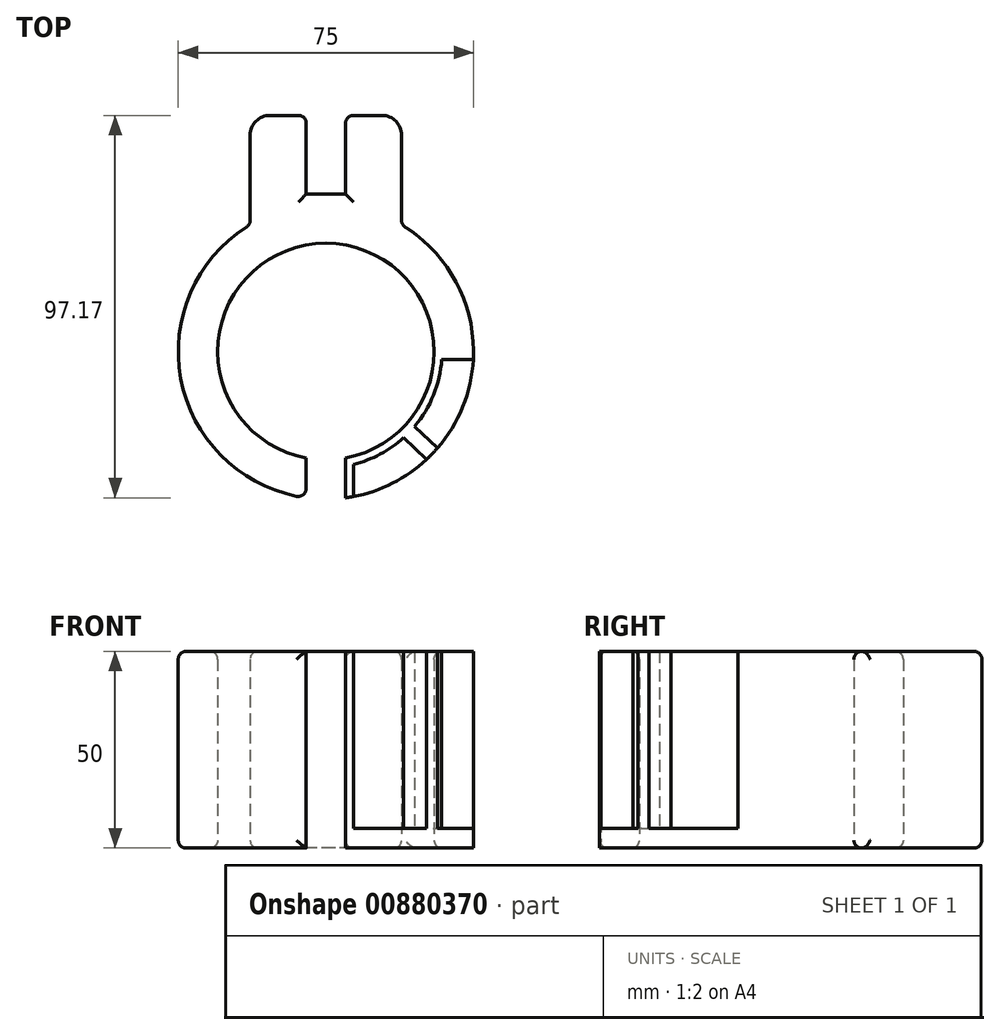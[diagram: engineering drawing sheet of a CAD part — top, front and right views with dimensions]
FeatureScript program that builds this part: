
annotation { "Feature Type Name" : "Feature", "Feature Type Description" : "" }
export const myFeature = defineFeature(function(context is Context, id is Id, definition is map)
    precondition{}
    {
        {
            var Q0;
            Q0=qCreatedBy(makeId("Top.planeOp"),FACE);
            var sketch = newSketch(context, id + "F0", { "sketchPlane" : qUnion([Q0])});
            skArc(sketch, "E0", {"start": v(-19.23, -27.8) * mm, "mid": v(-36.73, -67.54) * mm, "end": v(-5, -97.17) * mm});
            skLineSegment(sketch, "E1", {"start": v(-19.23, -5) * mm, "end": v(-19.23, -27.8) * mm});
            skLineSegment(sketch, "E2", {"start": v(-5, 0) * mm, "end": v(-5, -20) * mm});
            skLineSegment(sketch, "E3", {"start": v(-5, -20) * mm, "end": v(0, -20) * mm});
            skLineSegment(sketch, "E4", {"start": v(-14.23, 0) * mm, "end": v(-5, 0) * mm});
            skLineSegment(sketch, "E5.MirrorCS", {"start": v(19.23, -5) * mm, "end": v(19.23, -27.8) * mm});
            skLineSegment(sketch, "E6.MirrorCS", {"start": v(5, 0) * mm, "end": v(5, -20) * mm});
            skLineSegment(sketch, "E7.MirrorCS", {"start": v(14.23, 0) * mm, "end": v(5, 0) * mm});
            skLineSegment(sketch, "E8.MirrorCS", {"start": v(5, -20) * mm, "end": v(0, -20) * mm});
            skPoint(sketch, "E9.start.orphan", {"position": v(0, -22.5) * mm});
            skArc(sketch, "E10", {"start": v(5, -87.04) * mm, "mid": v(13.01, -84.23) * mm, "end": v(19.78, -79.1) * mm});
            skPoint(sketch, "E11.visualSharp", {"position": v(-19.23, 0) * mm});
            skArc(sketch, "E11.filletArc", {"start": v(-14.23, 0) * mm, "mid": v(-17.77, -1.46) * mm, "end": v(-19.23, -5) * mm});
            skPoint(sketch, "E12.visualSharp", {"position": v(19.23, 0) * mm});
            skArc(sketch, "E12.filletArc", {"start": v(19.23, -5) * mm, "mid": v(17.77, -1.46) * mm, "end": v(14.23, 0) * mm});
            skLineSegment(sketch, "E13", {"start": v(-5, -87.04) * mm, "end": v(-5, -97.17) * mm});
            skLineSegment(sketch, "E14.MirrorCS", {"start": v(5, -87.04) * mm, "end": v(5, -97.17) * mm});
            skArc(sketch, "E15.trimOffspring", {"start": v(5, -97.17) * mm, "mid": v(28.23, -84.69) * mm, "end": v(37.5, -60) * mm});
            skLineSegment(sketch, "E16", {"start": v(19.78, -79.1) * mm, "end": v(26.98, -86.05) * mm, "construction": true});
            skLineSegment(sketch, "E17.0", {"start": v(25.55, -87.45) * mm, "end": v(25.59, -87.48) * mm});
            skLineSegment(sketch, "E18.0", {"start": v(28.33, -84.57) * mm, "end": v(28.37, -84.6) * mm});
            skArc(sketch, "E19", {"start": v(19.78, -79.1) * mm, "mid": v(25.5, -70.3) * mm, "end": v(27.5, -60) * mm});
            skLineSegment(sketch, "E20.0", {"start": v(7, -88.66) * mm, "end": v(7, -96.84) * mm});
            skArc(sketch, "E20.1", {"start": v(7, -88.66) * mm, "mid": v(13.81, -86.07) * mm, "end": v(19.79, -81.88) * mm});
            skLineSegment(sketch, "E20.2", {"start": v(19.79, -81.88) * mm, "end": v(25.59, -87.48) * mm});
            skLineSegment(sketch, "E21", {"start": v(27.5, -60) * mm, "end": v(37.5, -60) * mm, "construction": true});
            skArc(sketch, "E22", {"start": v(27.5, -60) * mm, "mid": v(-17.59, -38.86) * mm, "end": v(-5, -87.04) * mm});
            skArc(sketch, "E23", {"start": v(37.5, -60) * mm, "mid": v(32.62, -41.5) * mm, "end": v(19.23, -27.8) * mm});
            skLineSegment(sketch, "E24.0", {"start": v(29.43, -62) * mm, "end": v(37.5, -62) * mm});
            skArc(sketch, "E24.1", {"start": v(22.56, -79) * mm, "mid": v(27.35, -71.05) * mm, "end": v(29.43, -62) * mm});
            skLineSegment(sketch, "E24.2", {"start": v(22.56, -79) * mm, "end": v(28.37, -84.6) * mm});
            skSolve(sketch);
        }
        {
            var Q0;
            Q0=makeQuery(id+"F0.imprint","IMPRINT",FACE,{"disambiguationData":[TD([[makeQuery(id+"F0.imprint","IMPRINT",EDGE,{"derivedFrom":sQuery(id+"F0.wireOp",EDGE,"E0")}),1.0]])]});
            extrude(context, id + "F1", {"entities" : qUnion([Q0]), "depth" : 50 * mm, "offsetDistance" : 25 * mm});
        }
        {
            var Q0;
            {var subQ0=sQuery(id+"F0.wireOp",EDGE,"E20.0");Q0=makeQuery(id+"F0.imprint","IMPRINT",FACE,{"disambiguationData":[TD([[makeQuery(id+"F0.imprint","IMPRINT",EDGE,{"derivedFrom":subQ0}),1.0]])]});}
            var Q1;
            {var subQ5=sQuery(id+"F0.wireOp",EDGE,"E24.1");Q1=makeQuery(id+"F0.imprint","IMPRINT",FACE,{"disambiguationData":[TD([[makeQuery(id+"F0.imprint","IMPRINT",EDGE,{"derivedFrom":subQ5}),-1.0]])]});}
            extrude(context, id + "F2", {"entities" : qUnion([Q0, Q1]), "operationType" : NewBodyOperationType.ADD, "depth" : 5 * mm, "offsetDistance" : 25 * mm});
        }
        {
            var Q0;
            Q0=makeQuery(id+"F1.opExtrude","CAP_EDGE",EDGE,{"disambiguationData":[OSD([sQuery(id+"F0.wireOp",EDGE,"E0")])],"isStart":false});
            var Q1;
            Q1=makeQuery(id+"F1.opExtrude","CAP_EDGE",EDGE,{"disambiguationData":[OSD([sQuery(id+"F0.wireOp",EDGE,"E5.MirrorCS")])],"isStart":false});
            var Q2;
            Q2=makeQuery(id+"F1.opExtrude","CAP_EDGE",EDGE,{"disambiguationData":[OSD([sQuery(id+"F0.wireOp",EDGE,"E1")])],"isStart":false});
            var Q3;
            Q3=makeQuery(id+"F1.opExtrude","CAP_EDGE",EDGE,{"disambiguationData":[OSD([sQuery(id+"F0.wireOp",EDGE,"E2")])],"isStart":false});
            var Q4;
            Q4=makeQuery(id+"F1.opExtrude","CAP_EDGE",EDGE,{"disambiguationData":[OSD([sQuery(id+"F0.wireOp",EDGE,"E3"),sQuery(id+"F0.wireOp",EDGE,"E8.MirrorCS")])],"isStart":false});
            var Q5;
            Q5=makeQuery(id+"F1.opExtrude","CAP_EDGE",EDGE,{"disambiguationData":[OSD([sQuery(id+"F0.wireOp",EDGE,"E6.MirrorCS")])],"isStart":false});
            var Q6;
            Q6=makeQuery(id+"F1.opExtrude","SWEPT_EDGE",EDGE,{"disambiguationData":[OSD([sQuery(id+"F0.wireOp",EDGE,"E6.MirrorCS"),sQuery(id+"F0.wireOp",EDGE,"E7.MirrorCS")])]});
            var Q7;
            Q7=makeQuery(id+"F1.opExtrude","SWEPT_EDGE",EDGE,{"disambiguationData":[OSD([sQuery(id+"F0.wireOp",EDGE,"E2"),sQuery(id+"F0.wireOp",EDGE,"E4")])]});
            var Q8;
            Q8=makeQuery(id+"F1.opExtrude","CAP_EDGE",EDGE,{"disambiguationData":[OSD([sQuery(id+"F0.wireOp",EDGE,"E5.MirrorCS")])],"isStart":true});
            var Q9;
            Q9=makeQuery(id+"F1.opExtrude","CAP_EDGE",EDGE,{"disambiguationData":[OSD([sQuery(id+"F0.wireOp",EDGE,"E6.MirrorCS")])],"isStart":true});
            var Q10;
            Q10=makeQuery(id+"F1.opExtrude","CAP_EDGE",EDGE,{"disambiguationData":[OSD([sQuery(id+"F0.wireOp",EDGE,"E3"),sQuery(id+"F0.wireOp",EDGE,"E8.MirrorCS")])],"isStart":true});
            var Q11;
            Q11=makeQuery(id+"F1.opExtrude","CAP_EDGE",EDGE,{"disambiguationData":[OSD([sQuery(id+"F0.wireOp",EDGE,"E2")])],"isStart":true});
            var Q12;
            Q12=makeQuery(id+"F1.opExtrude","CAP_EDGE",EDGE,{"disambiguationData":[OSD([sQuery(id+"F0.wireOp",EDGE,"E1")])],"isStart":true});
            var Q13;
            Q13=makeQuery(id+"F1.opExtrude","CAP_EDGE",EDGE,{"disambiguationData":[OSD([sQuery(id+"F0.wireOp",EDGE,"E0")])],"isStart":true});
            var Q14;
            Q14=makeQuery(id+"F1.opExtrude","CAP_EDGE",EDGE,{"disambiguationData":[OSD([sQuery(id+"F0.wireOp",EDGE,"E10")])],"isStart":false});
            var Q15;
            Q15=makeQuery(id+"F1.opExtrude","CAP_EDGE",EDGE,{"disambiguationData":[OSD([sQuery(id+"F0.wireOp",EDGE,"E10")])],"isStart":true});
            var Q16;
            Q16=makeQuery(id+"F1.opExtrude","SWEPT_EDGE",EDGE,{"disambiguationData":[OSD([sQuery(id+"F0.wireOp",EDGE,"E0"),sQuery(id+"F0.wireOp",EDGE,"E1")])]});
            var Q17;
            Q17=makeQuery(id+"F1.opExtrude","SWEPT_EDGE",EDGE,{"disambiguationData":[OSD([sQuery(id+"F0.wireOp",EDGE,"E0"),sQuery(id+"F0.wireOp",EDGE,"E5.MirrorCS")])]});
            fillet(context, id + "F3", {"entities" : qUnion([Q0, Q1, Q2, Q3, Q4, Q5, Q6, Q7, Q8, Q9, Q10, Q11, Q12, Q13, Q14, Q15, Q16, Q17]), "radius" : 2 * mm, "tangentPropagation" : true, "allowEdgeOverflow" : false});
        }
    });
